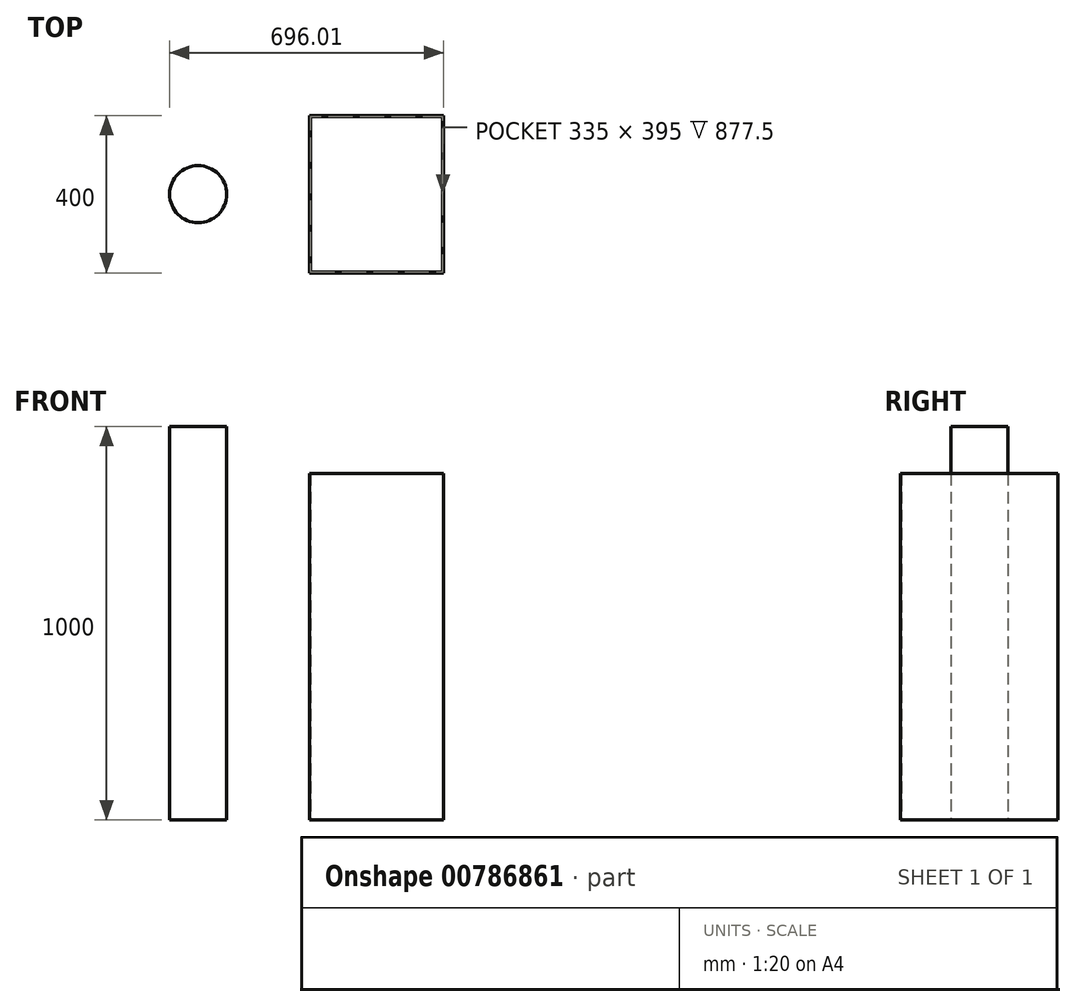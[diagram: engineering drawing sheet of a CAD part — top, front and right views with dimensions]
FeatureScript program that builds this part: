
annotation { "Feature Type Name" : "Feature", "Feature Type Description" : "" }
export const myFeature = defineFeature(function(context is Context, id is Id, definition is map)
    precondition{}
    {
        {
            var Q0;
            Q0=qCreatedBy(makeId("Top.planeOp"),FACE);
            var sketch = newSketch(context, id + "F0", { "sketchPlane" : qUnion([Q0])});
            skLineSegment(sketch, "E0.bottom", {"start": v(-170, -200) * mm, "end": v(170, -200) * mm});
            skLineSegment(sketch, "E0.top", {"start": v(-170, 200) * mm, "end": v(170, 200) * mm});
            skLineSegment(sketch, "E0.left", {"start": v(-170, -200) * mm, "end": v(-170, 200) * mm});
            skLineSegment(sketch, "E0.right", {"start": v(170, -200) * mm, "end": v(170, 200) * mm});
            skPoint(sketch, "E0.middle", {"position": v(0, 0) * mm});
            skSolve(sketch);
        }
        {
            var Q0;
            Q0 = qSketchRegion(id + "F0", true);
            extrude(context, id + "F1", {"entities" : qUnion([Q0]), "depth" : 880 * mm, "offsetDistance" : 25 * mm});
        }
        {
            var Q0;
            Q0=makeQuery(id+"F1.opExtrude","CAP_FACE",FACE,{"disambiguationData":[OSD([sQuery(id+"F0.wireOp",EDGE,"E0.bottom"),sQuery(id+"F0.wireOp",EDGE,"E0.top"),sQuery(id+"F0.wireOp",EDGE,"E0.left"),sQuery(id+"F0.wireOp",EDGE,"E0.right")])],"isStart":false});
            shell(context, id + "F2", {"entities" : qUnion([Q0]), "thickness" : 2.5 * mm});
        }
        {
            var Q0;
            Q0=makeQuery(id+"F0.imprint","IMPRINT",FACE,{"disambiguationData":[TD([[makeQuery(id+"F0.imprint","IMPRINT",EDGE,{"derivedFrom":sQuery(id+"F0.wireOp",EDGE,"E0.bottom")}),1.0]])]});
            var sketch = newSketch(context, id + "F3", { "sketchPlane" : qUnion([Q0])});
            skLineSegment(sketch, "E1.bottom", {"start": v(-695.01, -140) * mm, "end": v(-212.01, -140) * mm});
            skLineSegment(sketch, "E1.top", {"start": v(-695.01, 140) * mm, "end": v(-212.01, 140) * mm});
            skLineSegment(sketch, "E1.left", {"start": v(-695.01, -140) * mm, "end": v(-695.01, 140) * mm});
            skLineSegment(sketch, "E1.right", {"start": v(-212.01, -140) * mm, "end": v(-212.01, 140) * mm});
            skPoint(sketch, "E1.middle", {"position": v(-453.51, 0) * mm});
            skCircle(sketch, "E2", {"center": v(-453.51, 0) * mm, "radius": 72.5 * mm});
            skSolve(sketch);
        }
        {
            var Q0;
            Q0=makeQuery(id+"F3.imprint","IMPRINT",FACE,{"disambiguationData":[TD([[makeQuery(id+"F3.imprint","IMPRINT",EDGE,{"derivedFrom":sQuery(id+"F3.wireOp",EDGE,"E2")}),1.0]])]});
            extrude(context, id + "F4", {"entities" : qUnion([Q0]), "depth" : 1000 * mm, "offsetDistance" : 25 * mm});
        }
    });
